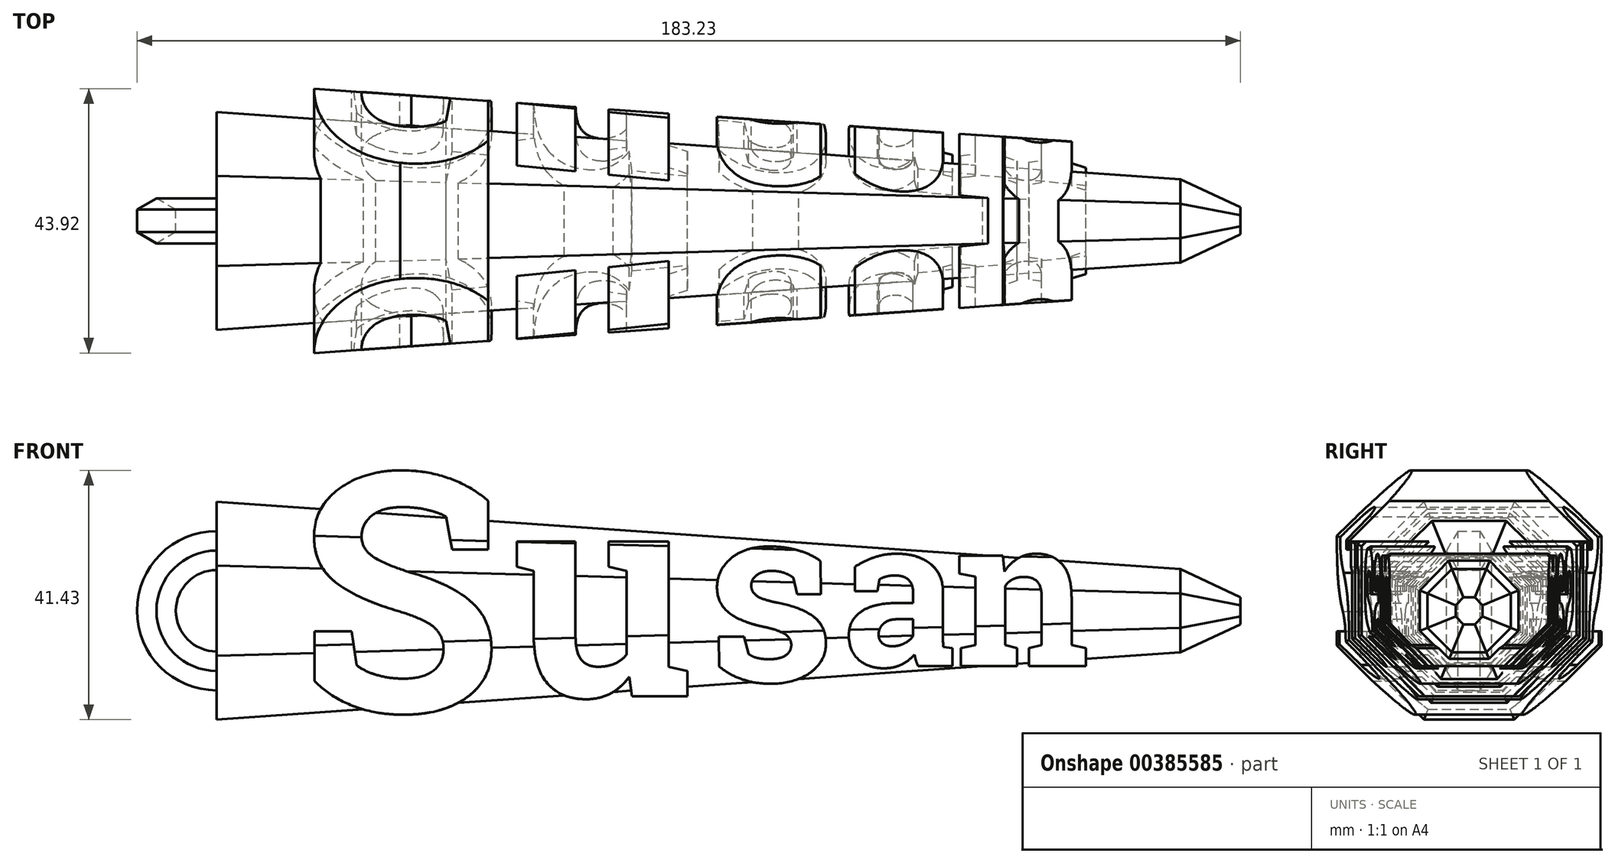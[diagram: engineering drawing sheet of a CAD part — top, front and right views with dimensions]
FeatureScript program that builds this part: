
annotation { "Feature Type Name" : "Feature", "Feature Type Description" : "" }
export const myFeature = defineFeature(function(context is Context, id is Id, definition is map)
    precondition{}
    {
        {
            assignVariable(context, id + "F0", {"name" : "hookPlane", "anyValue" : 80});
        }
        {
            assignVariable(context, id + "F1", {"name" : "halfLength", "anyValue" : 80});
        }
        {
            var Q0;
            Q0=qCreatedBy(makeId("Front.planeOp"),FACE);
            var sketch = newSketch(context, id + "F2", { "sketchPlane" : qUnion([Q0])});
            skText(sketch, "E0", { "text": "S", "fontName": "RobotoSlab-Bold.ttf"});
            skPoint(sketch, "E1", {"position": v(-30.96, 0) * mm});
            skText(sketch, "E2", { "text": "u", "fontName": "RobotoSlab-Bold.ttf"});
            skText(sketch, "E3", { "text": "s", "fontName": "RobotoSlab-Bold.ttf"});
            skText(sketch, "E4", { "text": "an", "fontName": "RobotoSlab-Bold.ttf"});
            skPoint(sketch, "E5", {"position": v(1.11, 0) * mm});
            skPoint(sketch, "E6", {"position": v(23.72, 0) * mm});
            skLineSegment(sketch, "E7", {"start": v(-66.46, -20) * mm, "end": v(-66.46, -51.65) * mm, "construction": true});
            skLineSegment(sketch, "E8", {"start": v(-66.46, -51.65) * mm, "end": v(66.46, -51.65) * mm, "construction": true});
            skLineSegment(sketch, "E9", {"start": v(66.46, -51.65) * mm, "end": v(66.46, -12.5) * mm, "construction": true});
            skPoint(sketch, "E10", {"position": v(0, -51.65) * mm});
            const initialGuessF2  = {"E0": [-0.06646, -0.02, 1, 0, 0.04], "E2": [-0.03096, -0.0175, 1, 0, 0.035], "E3": [0.00111, -0.015, 1, 0, 0.03], "E4": [0.02372, -0.0125, 1, 0, 0.025]};
            skSetInitialGuess(sketch, initialGuessF2);
            skSolve(sketch);
        }
        {
            var Q0;
            Q0=qSketchRegion(id+"F2",true);
            extrude(context, id + "F3", {"entities" : qUnion([Q0]), "depth" : 25 * mm, "hasSecondDirection" : true, "secondDirectionOppositeDirection" : true, "secondDirectionDepth" : 25 * mm});
        }
        {
            var Q0;
            Q0=qCreatedBy(makeId("Right.planeOp"),FACE);
            var sketch = newSketch(context, id + "F4", { "sketchPlane" : qUnion([Q0])});
            skCircle(sketch, "E11", {"center": v(0, -3.3) * mm, "radius": 12.5 * mm, "construction": true});
            skLineSegment(sketch, "E12", {"start": v(0, 16.7) * mm, "end": v(0, 12.95) * mm, "construction": true});
            skLineSegment(sketch, "E13.0", {"start": v(-5.18, 9.2) * mm, "end": v(5.18, 9.2) * mm});
            skLineSegment(sketch, "E13.1", {"start": v(5.18, 9.2) * mm, "end": v(12.5, 1.88) * mm});
            skLineSegment(sketch, "E13.2", {"start": v(12.5, 1.88) * mm, "end": v(12.5, -8.47) * mm});
            skLineSegment(sketch, "E13.3", {"start": v(12.5, -8.47) * mm, "end": v(5.18, -15.8) * mm});
            skLineSegment(sketch, "E13.4", {"start": v(5.18, -15.8) * mm, "end": v(-5.18, -15.8) * mm});
            skLineSegment(sketch, "E13.5", {"start": v(-5.18, -15.8) * mm, "end": v(-12.5, -8.47) * mm});
            skLineSegment(sketch, "E13.6", {"start": v(-12.5, -8.47) * mm, "end": v(-12.5, 1.88) * mm});
            skLineSegment(sketch, "E13.7", {"start": v(-12.5, 1.88) * mm, "end": v(-5.18, 9.2) * mm});
            skPoint(sketch, "E13.0.midPoint", {"position": v(0, 9.2) * mm});
            skLineSegment(sketch, "E14", {"start": v(0, 16.7) * mm, "end": v(0, 9.2) * mm});
            skSolve(sketch);
        }
        {
            var Q0;
            Q0=qSketchRegion(id+"F4",true);
            var Q1;
            Q1=makeQuery(id+"F3.opExtrude","SWEPT_FACE",FACE,{"disambiguationData":[OSD([sQuery(id+"F2.wireOp",EDGE,"E4.sketch_text.stroke-1")])]});
            extrude(context, id + "F5", {"entities" : qUnion([Q0]), "operationType" : NewBodyOperationType.ADD, "oppositeDirection" : true, "depth" : (getVariable(context, 'halfLength')) * mm, "hasDraft" : true, "draftAngle" : 4 * degree, "hasSecondDirection" : true, "secondDirectionOppositeDirection" : false, "secondDirectionBoundEntityFace" : qUnion([Q1]), "secondDirectionDepth" : (getVariable(context, 'halfLength')) * mm, "hasSecondDirectionDraft" : true, "secondDirectionDraftAngle" : 4 * degree, "secondDirectionDraftPullDirection" : true});
        }
        {
            var Q0;
            Q0=qCreatedBy(makeId("Right.planeOp"),FACE);
            var sketch = newSketch(context, id + "F6", { "sketchPlane" : qUnion([Q0])});
            skCircle(sketch, "E15.cCircle", {"center": v(0, 0.04) * mm, "radius": 17.5 * mm, "construction": true});
            skLineSegment(sketch, "E15.0", {"start": v(-7.25, 17.54) * mm, "end": v(7.25, 17.54) * mm});
            skLineSegment(sketch, "E15.1", {"start": v(7.25, 17.54) * mm, "end": v(17.5, 7.3) * mm});
            skLineSegment(sketch, "E15.2", {"start": v(17.5, 7.3) * mm, "end": v(17.5, -7.2) * mm});
            skLineSegment(sketch, "E15.3", {"start": v(17.5, -7.2) * mm, "end": v(7.25, -17.46) * mm});
            skLineSegment(sketch, "E15.4", {"start": v(7.25, -17.46) * mm, "end": v(-7.25, -17.46) * mm});
            skLineSegment(sketch, "E15.5", {"start": v(-7.25, -17.46) * mm, "end": v(-17.5, -7.2) * mm});
            skLineSegment(sketch, "E15.6", {"start": v(-17.5, -7.2) * mm, "end": v(-17.5, 7.3) * mm});
            skLineSegment(sketch, "E15.7", {"start": v(-17.5, 7.3) * mm, "end": v(-7.25, 17.54) * mm});
            skLineSegment(sketch, "E16.bottom", {"start": v(37.5, 37.54) * mm, "end": v(-37.5, 37.54) * mm});
            skLineSegment(sketch, "E16.top", {"start": v(37.5, -37.46) * mm, "end": v(-37.5, -37.46) * mm});
            skLineSegment(sketch, "E16.left", {"start": v(37.5, 37.54) * mm, "end": v(37.5, -37.46) * mm});
            skLineSegment(sketch, "E16.right", {"start": v(-37.5, 37.54) * mm, "end": v(-37.5, -37.46) * mm});
            skLineSegment(sketch, "E17", {"start": v(0, 20.04) * mm, "end": v(0, -8.52) * mm, "construction": true});
            skSolve(sketch);
        }
        {
            var Q0;
            Q0=makeQuery(id+"F6.imprint","IMPRINT",FACE,{"disambiguationData":[TD([[makeQuery(id+"F6.imprint","IMPRINT",EDGE,{"derivedFrom":sQuery(id+"F6.wireOp",EDGE,"E15.0")}),1.0]])]});
            extrude(context, id + "F7", {"entities" : qUnion([Q0]), "operationType" : NewBodyOperationType.REMOVE, "endBound" : BoundingType.THROUGH_ALL, "depth" : 25 * mm, "hasDraft" : true, "draftAngle" : 4 * degree, "hasSecondDirection" : true, "secondDirectionBound" : SecondDirectionBoundingType.THROUGH_ALL, "secondDirectionOppositeDirection" : true, "secondDirectionDepth" : 25 * mm, "hasSecondDirectionDraft" : true, "secondDirectionDraftAngle" : 4 * degree, "secondDirectionDraftPullDirection" : true});
        }
        {
            var Q0;
            {var subQ0=sQuery(id+"F4.wireOp",EDGE,"E13.3");var subQ1=sQuery(id+"F4.wireOp",EDGE,"E13.2");var subQ2=sQuery(id+"F4.wireOp",EDGE,"E13.4");var subQ3=sQuery(id+"F4.wireOp",EDGE,"E13.5");var subQ4=sQuery(id+"F4.wireOp",EDGE,"E13.6");Q0=makeQuery(id+"F5.boolean.opBoolean","SPLIT",FACE,{"disambiguationData":[TD([makeQuery(id+"F3.opExtrude","SWEPT_FACE",FACE,{"disambiguationData":[OSD([sQuery(id+"F2.wireOp",EDGE,"E4.sketch_text.stroke-0")])]})])],"derivedFrom":makeQuery(id+"F5.opExtrude","CAP_FACE",FACE,{"disambiguationData":[OSD([sQuery(id+"F4.wireOp",EDGE,"E13.0"),sQuery(id+"F4.wireOp",EDGE,"E13.1"),subQ1,subQ0,subQ2,subQ3,subQ4,sQuery(id+"F4.wireOp",EDGE,"E13.7")])],"isStart":true})});}
            var sketch = newSketch(context, id + "F8", { "sketchPlane" : qUnion([Q0])});
            skCircle(sketch, "E18.cCircle", {"center": v(0, -3.3) * mm, "radius": 6.9 * mm, "construction": true});
            skLineSegment(sketch, "E18.0", {"start": v(-2.86, 3.6) * mm, "end": v(2.86, 3.6) * mm});
            skLineSegment(sketch, "E18.1", {"start": v(2.86, 3.6) * mm, "end": v(6.9, -0.44) * mm});
            skLineSegment(sketch, "E18.2", {"start": v(6.9, -0.44) * mm, "end": v(6.9, -6.16) * mm});
            skLineSegment(sketch, "E18.3", {"start": v(6.9, -6.16) * mm, "end": v(2.86, -10.2) * mm});
            skLineSegment(sketch, "E18.4", {"start": v(2.86, -10.2) * mm, "end": v(-2.86, -10.2) * mm});
            skLineSegment(sketch, "E18.5", {"start": v(-2.86, -10.2) * mm, "end": v(-6.9, -6.16) * mm});
            skLineSegment(sketch, "E18.6", {"start": v(-6.9, -6.16) * mm, "end": v(-6.9, -0.44) * mm});
            skLineSegment(sketch, "E18.7", {"start": v(-6.9, -0.44) * mm, "end": v(-2.86, 3.6) * mm});
            skPoint(sketch, "E18.0.midPoint", {"position": v(0, 3.6) * mm});
            skLineSegment(sketch, "E19", {"start": v(0, 19.59) * mm, "end": v(0, -20.57) * mm, "construction": true});
            skSolve(sketch);
        }
        {
            var Q0;
            Q0=qSketchRegion(id+"F8",true);
            extrude(context, id + "F9", {"entities" : qUnion([Q0]), "operationType" : NewBodyOperationType.ADD, "depth" : 10 * mm, "hasDraft" : true, "draftAngle" : 25 * degree, "draftPullDirection" : true});
        }
        {
            var Q0;
            Q0=qCreatedBy(makeId("Right.planeOp"),FACE);
            cPlane(context, id + "F10", {"entities" : qUnion([Q0]), "cplaneType" : CPlaneType.OFFSET, "offset" : (getVariable(context, 'hookPlane')) * mm, "oppositeDirection" : true, "width" : 150 * mm, "height" : 150 * mm});
        }
        {
            var Q0;
            Q0=qCreatedBy(makeId("Front.planeOp"),FACE);
            var sketch = newSketch(context, id + "F11", { "sketchPlane" : qUnion([Q0])});
            skArc(sketch, "E20", {"start": v(-73.39, 4.2) * mm, "mid": v(-90, -3.3) * mm, "end": v(-73.39, -10.8) * mm});
            skLineSegment(sketch, "E21", {"start": v(-73.39, 4.2) * mm, "end": v(-73.39, -10.8) * mm, "construction": true});
            skPoint(sketch, "E22", {"position": v(-73.39, -3.3) * mm});
            skLineSegment(sketch, "E23", {"start": v(-80, 14.8) * mm, "end": v(-80, -21.4) * mm, "construction": true});
            skSolve(sketch);
        }
        {
            var Q0;
            Q0=qCreatedBy(id+"F10.planeOp",FACE);
            var sketch = newSketch(context, id + "F12", { "sketchPlane" : qUnion([Q0])});
            skCircle(sketch, "E24.cCircle", {"center": v(0, 6.7) * mm, "radius": 3.23 * mm, "construction": true});
            skLineSegment(sketch, "E24.0", {"start": v(1.87, 3.47) * mm, "end": v(-1.87, 3.47) * mm});
            skLineSegment(sketch, "E24.1", {"start": v(-1.87, 3.47) * mm, "end": v(-3.73, 6.7) * mm});
            skLineSegment(sketch, "E24.2", {"start": v(-3.73, 6.7) * mm, "end": v(-1.87, 9.94) * mm});
            skLineSegment(sketch, "E24.3", {"start": v(-1.87, 9.94) * mm, "end": v(1.87, 9.94) * mm});
            skLineSegment(sketch, "E24.4", {"start": v(1.87, 9.94) * mm, "end": v(3.73, 6.7) * mm});
            skLineSegment(sketch, "E24.5", {"start": v(3.73, 6.7) * mm, "end": v(1.87, 3.47) * mm});
            skPoint(sketch, "E24.0.midPoint", {"position": v(0, 3.47) * mm});
            skSolve(sketch);
        }
        {
            var Q0;
            Q0=qSketchRegion(id+"F12",true);
            var Q1;
            Q1=qConstructionFilter(qBodyType(qCreatedBy(id+"F11",EDGE),BodyType.WIRE),ConstructionObject.NO);
            sweep(context, id + "F13", {"operationType" : NewBodyOperationType.ADD, "profiles" : qUnion([Q0]), "path" : qUnion([Q1])});
        }
    });
